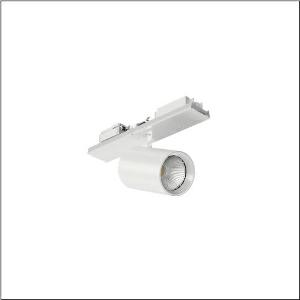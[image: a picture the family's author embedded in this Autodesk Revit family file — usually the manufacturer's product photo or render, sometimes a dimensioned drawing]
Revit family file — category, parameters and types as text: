
# Revit family: licross_spot_31_51sl13da45b
name_source: partatom
category: Lighting Fixtures
units: mm (PartAtom-declared; Revit-internal decimal feet)

## family parameters
Cut with Voids When Loaded = No
Host = Face
Light Source = No
Part Type = Normal
Room Calculation Point = No
Round Connector Dimension = Use Diameter
Shared = No

## types (1)
- --- (1 x LED, 5190 lm, 43.9 W, 4000K)
    Apparent Load = 44 VA
    CIE Flux Codes = 92 97 99 100 100
    Color Rendering = 90
    Color Temperature = 4000K
    Default Elevation = 1800 mm
    Description = Licross Spot 31, directional spotlight, light control with lens, of plastic, LED rated luminous flux: 5.190lm, light colour: 940, with plug, 5-pole, mains connection: 220..240V, AC, 50/60Hz, of aluminium, traffic white (RAL 9016), length: 300mm, diameter: 90mm, protection rating (complete): IP20, insulation class (complete): insulation class I (protective earthing), certification: CE, packaging unit: 1 piece
    Height = 175 mm
    Lamp = 1 x LED
    Lamp Light Flux = 5190 lm
    Lamp Power = 43.9 W
    Lamp count = 1
    Length = 90 mm
    Luminous efficacy = 118 lm/W
    Manufacturer = Siteco
    ModVariant = No
    Model = 51SL13DA45B
    Mounting Place = Ceiling
    Mounting Type = Pendant
    Number of Poles = 1
    OnlyDefault = Yes
    Power Factor = 1
    Product Name = Licross Spot 31
    Product group = directional spotlight
    ProductGroupID = 905
    Protection Class = Protection class I
    Protection Degree = IP 20
    RLX_Detail_Level = 1
    RLX_Emergency_Light_Flux = 0 lm
    RLX_Emergency_Type = 0
    RLX_Emergency_Type_DB = No
    RlxData = <blob elided: 14765 chars, md5=7f84125e>
    Socket = socket
    Standby Power = 0 W
    System Light Flux = 5190 lm
    System Power = 44 W
    Type Comments = factory setting: luminous flux: 100 % | (ON | ON | ON) | 1050 mA
    Type Image = l_1245720.jpg
    URL = http://relux.com
    VarID = @adj_133229
    Voltage = 0 V
    Weight = 0.00 kg
    Width = 0 mm  [stored 0 ft]

note: [stored X ft] marks values corroborated as IEEE doubles in the binary element streams (Revit-internal decimal feet)

## geometry (parser evidence)
native form markers: Sweep x13
no freeform markers — native parametric forms only
